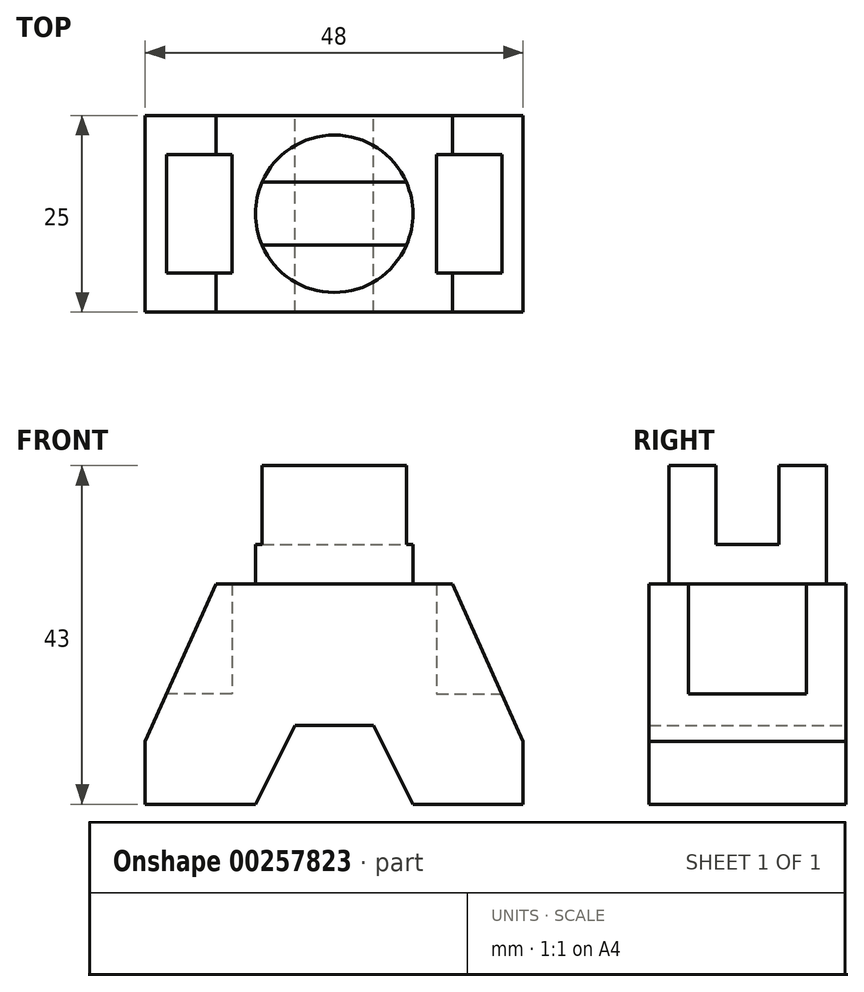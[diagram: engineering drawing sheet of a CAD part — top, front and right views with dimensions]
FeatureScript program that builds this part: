
annotation { "Feature Type Name" : "Feature", "Feature Type Description" : "" }
export const myFeature = defineFeature(function(context is Context, id is Id, definition is map)
    precondition{}
    {
        {
            var Q0;
            Q0=qCreatedBy(makeId("Front.planeOp"),FACE);
            var sketch = newSketch(context, id + "F0", { "sketchPlane" : qUnion([Q0])});
            skLineSegment(sketch, "E0.bottom", {"start": v(-24, 28) * mm, "end": v(24, 28) * mm});
            skLineSegment(sketch, "E0.top", {"start": v(-24, 0) * mm, "end": v(24, 0) * mm});
            skLineSegment(sketch, "E0.left", {"start": v(-24, 28) * mm, "end": v(-24, 0) * mm});
            skLineSegment(sketch, "E0.right", {"start": v(24, 28) * mm, "end": v(24, 0) * mm});
            skLineSegment(sketch, "E1", {"start": v(-10, 0) * mm, "end": v(-5, 10) * mm});
            skLineSegment(sketch, "E2", {"start": v(-5, 10) * mm, "end": v(5, 10) * mm});
            skLineSegment(sketch, "E3", {"start": v(5, 10) * mm, "end": v(10, 0) * mm});
            skSolve(sketch);
        }
        {
            var Q0;
            Q0=makeQuery(id+"F0.imprint","IMPRINT",FACE,{"disambiguationData":[TD([[makeQuery(id+"F0.imprint","IMPRINT",EDGE,{"derivedFrom":sQuery(id+"F0.wireOp",EDGE,"E0.bottom")}),-1.0]])]});
            extrude(context, id + "F1", {"entities" : qUnion([Q0]), "depth" : 25 * mm});
        }
        {
            var Q0;
            Q0=makeQuery(id+"F1.opExtrude","SWEPT_EDGE",EDGE,{"disambiguationData":[OSD([sQuery(id+"F0.wireOp",EDGE,"E0.bottom"),sQuery(id+"F0.wireOp",EDGE,"E0.left")])]});
            var Q1;
            Q1=makeQuery(id+"F1.opExtrude","SWEPT_EDGE",EDGE,{"disambiguationData":[OSD([sQuery(id+"F0.wireOp",EDGE,"E0.bottom"),sQuery(id+"F0.wireOp",EDGE,"E0.right")])]});
            chamfer(context, id + "F2", {"entities" : qUnion([Q0, Q1]), "chamferType" : ChamferType.TWO_OFFSETS, "width1" : 20 * mm, "oppositeDirection" : false, "width2" : 9 * mm, "tangentPropagation" : true});
        }
        {
            var Q0;
            Q0=makeQuery(id+"F1.opExtrude","SWEPT_FACE",FACE,{"disambiguationData":[OSD([sQuery(id+"F0.wireOp",EDGE,"E0.bottom")])]});
            var sketch = newSketch(context, id + "F3", { "sketchPlane" : qUnion([Q0])});
            skCircle(sketch, "E4", {"center": v(0, -12.5) * mm, "radius": 10 * mm});
            skSolve(sketch);
        }
        {
            var Q0;
            Q0=makeQuery(id+"F3.imprint","IMPRINT",FACE,{"disambiguationData":[TD([[makeQuery(id+"F3.imprint","IMPRINT",EDGE,{"derivedFrom":sQuery(id+"F3.wireOp",EDGE,"E4")}),1.0]])]});
            extrude(context, id + "F4", {"entities" : qUnion([Q0]), "operationType" : NewBodyOperationType.ADD, "depth" : 15 * mm});
        }
        {
            var Q0;
            Q0=makeQuery(id+"F4.opExtrude","CAP_FACE",FACE,{"disambiguationData":[OSD([sQuery(id+"F3.wireOp",EDGE,"E4")])],"isStart":false});
            var sketch = newSketch(context, id + "F5", { "sketchPlane" : qUnion([Q0])});
            skLineSegment(sketch, "E5", {"start": v(-9.17, -8.5) * mm, "end": v(9.17, -8.5) * mm});
            skLineSegment(sketch, "E6", {"start": v(-9.17, -16.5) * mm, "end": v(9.17, -16.5) * mm});
            skSolve(sketch);
        }
        {
            var Q0;
            {var subQ0=sQuery(id+"F5.wireOp",EDGE,"E5");Q0=makeQuery(id+"F5.imprint","IMPRINT",FACE,{"disambiguationData":[TD([[makeQuery(id+"F5.imprint","IMPRINT",EDGE,{"derivedFrom":subQ0}),-1.0]])]});}
            extrude(context, id + "F6", {"entities" : qUnion([Q0]), "operationType" : NewBodyOperationType.REMOVE, "oppositeDirection" : true, "depth" : 10 * mm});
        }
        {
            var Q0;
            Q0=makeQuery(id+"F1.opExtrude","SWEPT_FACE",FACE,{"disambiguationData":[OSD([sQuery(id+"F0.wireOp",EDGE,"E0.right")])]});
            var sketch = newSketch(context, id + "F7", { "sketchPlane" : qUnion([Q0])});
            skLineSegment(sketch, "E7.bottom", {"start": v(-20, 28) * mm, "end": v(-5, 28) * mm});
            skLineSegment(sketch, "E7.top", {"start": v(-20, 14) * mm, "end": v(-5, 14) * mm});
            skLineSegment(sketch, "E7.left", {"start": v(-20, 28) * mm, "end": v(-20, 14) * mm});
            skLineSegment(sketch, "E7.right", {"start": v(-5, 28) * mm, "end": v(-5, 14) * mm});
            skSolve(sketch);
        }
        {
            var Q0;
            Q0 = qSketchRegion(id + "F7", true);
            extrude(context, id + "F8", {"entities" : qUnion([Q0]), "operationType" : NewBodyOperationType.REMOVE, "oppositeDirection" : true, "depth" : ((48 - (30 - 4)) / 2) * mm});
        }
        {
            var Q0;
            Q0=makeQuery(id+"F1.opExtrude","SWEPT_FACE",FACE,{"disambiguationData":[OSD([sQuery(id+"F0.wireOp",EDGE,"E0.left")])]});
            var sketch = newSketch(context, id + "F9", { "sketchPlane" : qUnion([Q0])});
            skLineSegment(sketch, "E8.bottom", {"start": v(5, 28) * mm, "end": v(20, 28) * mm});
            skLineSegment(sketch, "E8.top", {"start": v(5, 14) * mm, "end": v(20, 14) * mm});
            skLineSegment(sketch, "E8.left", {"start": v(5, 28) * mm, "end": v(5, 14) * mm});
            skLineSegment(sketch, "E8.right", {"start": v(20, 28) * mm, "end": v(20, 14) * mm});
            skSolve(sketch);
        }
        {
            var Q0;
            Q0 = qSketchRegion(id + "F9", true);
            extrude(context, id + "F10", {"entities" : qUnion([Q0]), "operationType" : NewBodyOperationType.REMOVE, "oppositeDirection" : true, "depth" : ((48 - (30 - 4)) / 2) * mm});
        }
    });
